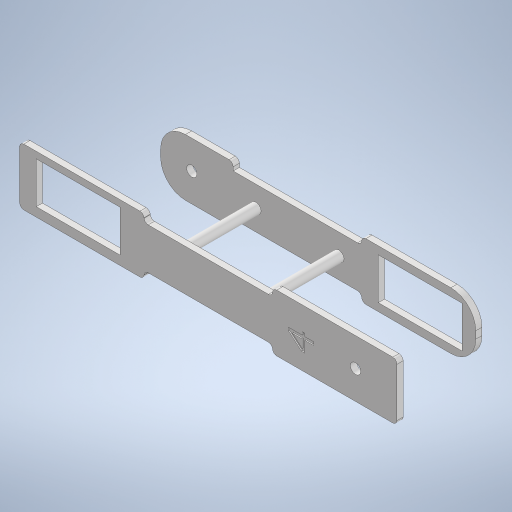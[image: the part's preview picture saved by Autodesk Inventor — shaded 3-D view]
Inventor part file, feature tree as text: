
AUTODESK INVENTOR PART (.ipt)
format: ipt  version: 2023 (Build 270158000, 158)  size: 396,800 bytes
history: native  units: mm
features: extrude x10, sketch x10, plane x2, other x1
ambient origin geometry x8: Origin, YZ Plane, XZ Plane, XY Plane, X Axis, Y Axis, Z Axis, Center Point
bodies: Body1 (feature_tree)
feature tree (23):
  other  "Sólido1"
  extrude  "Extrusión1"  Depth=60.0mm
  extrude  "Extrusión2"  Depth=20.0mm
  plane  "Plano de trabajo1"
  extrude  "Extrusión3"  Depth=27.5mm
  extrude  "Extrusión4"  Depth=3.0mm TaperAngle=0.0deg
  extrude  "Extrusión5"  Depth=5.0mm
  extrude  "Extrusión6"  Depth=3.0mm TaperAngle=0.0deg
  plane  "Plano de trabajo2"
  extrude  "Extrusión7"  Depth=27.5mm
  extrude  "Extrusión8"  Depth=152.0mm
  extrude  "Extrusión9"  Depth=62.0mm
  extrude  "Extrusión10"  Depth=12.0mm
  sketch  "Boceto1"  dims[d0=182.0mm d1=60.0mm]
  sketch  "Boceto2"  dims[d3=27.5mm d4=20.0mm]
  sketch  "Boceto3"  dims[d5=2.0mm d6=27.5mm]
  sketch  "Boceto4"  dims[d7=2.0mm d8=3.0mm d9=0.0mm]
  sketch  "Boceto5"  dims[d10=5.0mm d11=5.0mm]
  sketch  "Boceto6"  dims[d12=40.0mm d13=3.0mm d14=0.0mm]
  sketch  "Boceto7"  dims[d15=40.0mm d16=27.5mm]
  sketch  "Boceto8"  dims[d17=27.5mm d18=152.0mm]
  sketch  "Boceto9"  dims[d19=55.0mm d21=62.0mm]
  sketch  "Boceto10"  dims[d22=20.0mm d23=12.0mm d24=2.0mm d25=3.0mm d26=0.0mm d27=3.0mm d28=0.0mm d32=40.0mm d34=5.0mm d35=5.0mm d36=3.0mm d37=0.0mm d38=5.0mm d39=20.0mm d40=3.0mm d41=0.0mm d42=46.0mm d43=0.0mm d44=0.5mm d45=0.0mm d46=40.0mm d47=40.4mm d48=20.0mm d49=8.0mm d50=10.0mm d51=0.0mm d52=40.4mm d53=20.0mm d54=8.0mm d55=3.0mm d56=0.0mm]
